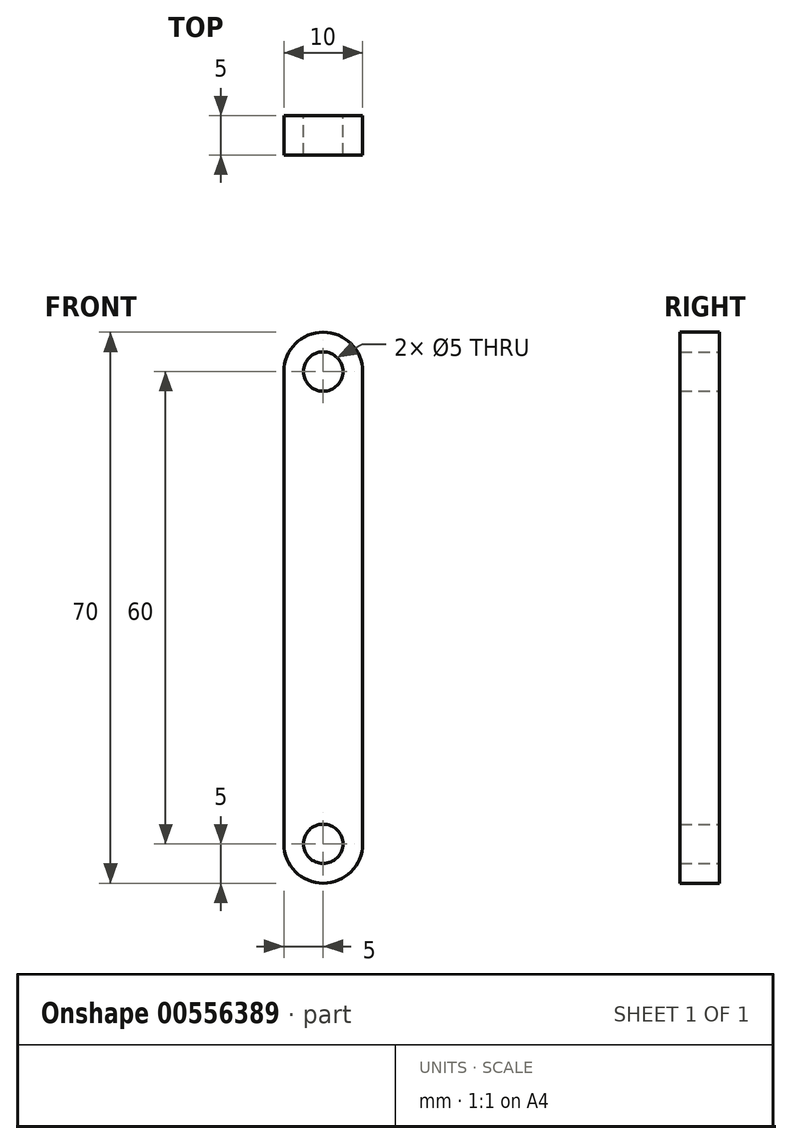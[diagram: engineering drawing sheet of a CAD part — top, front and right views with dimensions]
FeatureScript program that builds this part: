
annotation { "Feature Type Name" : "Feature", "Feature Type Description" : "" }
export const myFeature = defineFeature(function(context is Context, id is Id, definition is map)
    precondition{}
    {
        {
            var Q0;
            Q0=qCreatedBy(makeId("Front.planeOp"),FACE);
            var sketch = newSketch(context, id + "F0", { "sketchPlane" : qUnion([Q0])});
            skArc(sketch, "E0", {"start": v(-5, 0) * mm, "mid": v(0, -5) * mm, "end": v(5, 0) * mm});
            skCircle(sketch, "E1", {"center": v(0, 0) * mm, "radius": 2.5 * mm});
            skArc(sketch, "E2", {"start": v(5, 60) * mm, "mid": v(0, 65) * mm, "end": v(-5, 60) * mm});
            skCircle(sketch, "E3", {"center": v(0, 60) * mm, "radius": 2.5 * mm});
            skLineSegment(sketch, "E4", {"start": v(-5, 60) * mm, "end": v(-5, 0) * mm});
            skLineSegment(sketch, "E5", {"start": v(5, 60) * mm, "end": v(5, 0) * mm});
            skSolve(sketch);
        }
        {
            var Q0;
            Q0=makeQuery(id+"F0.imprint","IMPRINT",FACE,{"disambiguationData":[TD([[makeQuery(id+"F0.imprint","IMPRINT",EDGE,{"derivedFrom":sQuery(id+"F0.wireOp",EDGE,"E0")}),1.0]])]});
            extrude(context, id + "F1", {"entities" : qUnion([Q0]), "depth" : 5 * mm, "offsetDistance" : 25 * mm});
        }
    });
